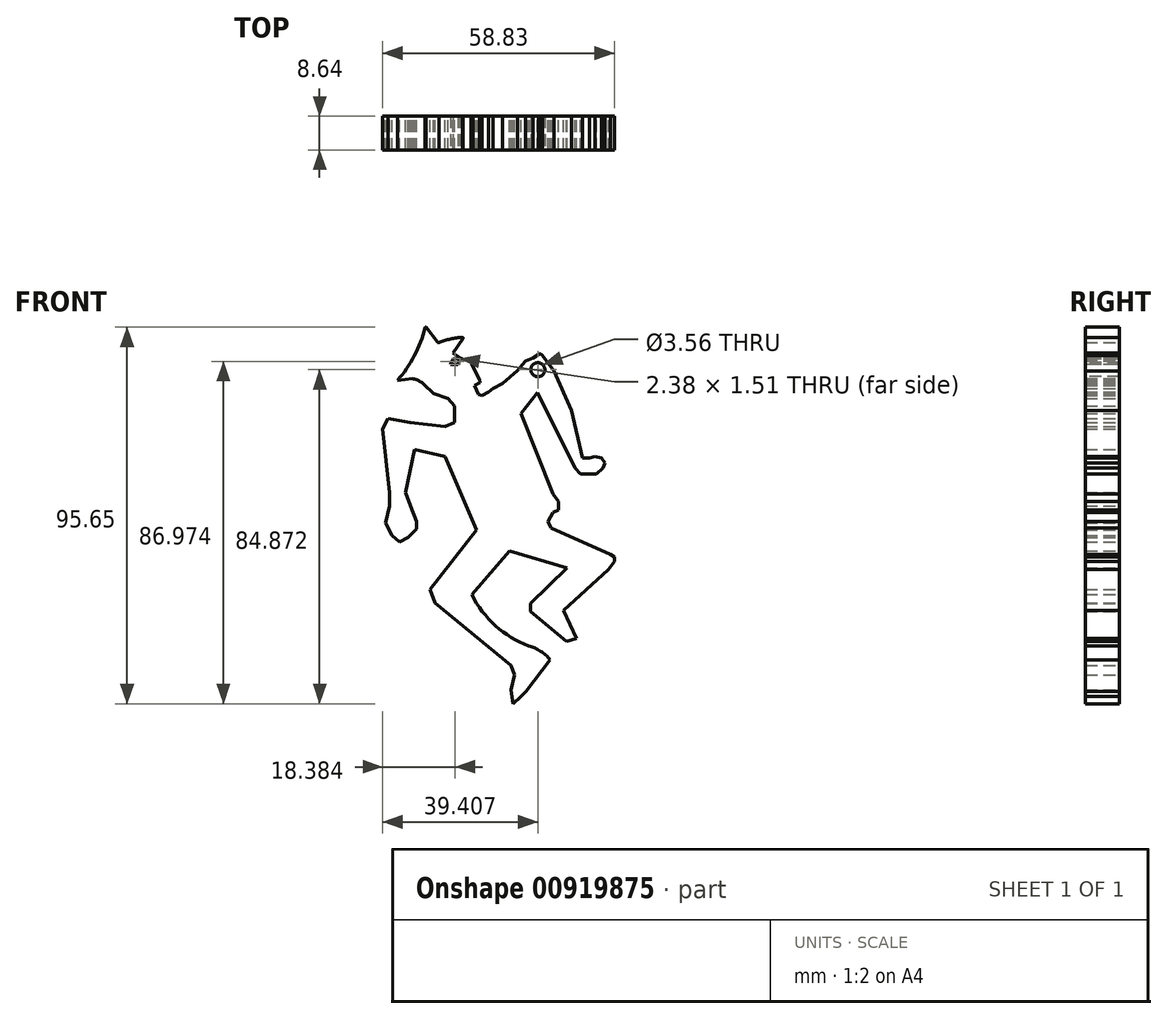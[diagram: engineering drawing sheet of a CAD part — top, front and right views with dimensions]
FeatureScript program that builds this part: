
annotation { "Feature Type Name" : "Feature", "Feature Type Description" : "" }
export const myFeature = defineFeature(function(context is Context, id is Id, definition is map)
    precondition{}
    {
        {
            var Q0;
            Q0=qCreatedBy(makeId("Front.planeOp"),FACE);
            var sketch = newSketch(context, id + "F0", { "sketchPlane" : qUnion([Q0])});
            skLineSegment(sketch, "E0", {"start": v(-42.46, 60.33) * mm, "end": v(-39.5, 56.54) * mm});
            skArc(sketch, "E1", {"start": v(-33.22, 57.79) * mm, "mid": v(-36.26, 57.36) * mm, "end": v(-39.19, 56.47) * mm});
            skLineSegment(sketch, "E2", {"start": v(-33.03, 57.41) * mm, "end": v(-35.53, 53.74) * mm});
            skLineSegment(sketch, "E3", {"start": v(-35.53, 53.74) * mm, "end": v(-33.9, 52.64) * mm});
            skArc(sketch, "E4", {"start": v(-33.9, 52.64) * mm, "mid": v(-32.51, 52.03) * mm, "end": v(-31, 51.97) * mm});
            skLineSegment(sketch, "E5", {"start": v(-30.57, 51.52) * mm, "end": v(-30.55, 51.48) * mm});
            skPoint(sketch, "E6.visualSharp", {"position": v(-29.06, 47.76) * mm});
            skPoint(sketch, "E7.visualSharp", {"position": v(-43.57, 61.76) * mm});
            skPoint(sketch, "E8.visualSharp", {"position": v(-39.37, 56.4) * mm});
            skLineSegment(sketch, "E8.filletArc", {"start": v(-39.5, 56.54) * mm, "end": v(-39.5, 56.54) * mm});
            skPoint(sketch, "E9.visualSharp", {"position": v(-32.76, 57.81) * mm});
            skArc(sketch, "E10", {"start": v(-49.73, 46.76) * mm, "mid": v(-45.43, 53.08) * mm, "end": v(-42.67, 60.2) * mm});
            skPoint(sketch, "E11.visualSharp", {"position": v(-45.9, 47.27) * mm});
            skPoint(sketch, "E12.start.orphan", {"position": v(-40.55, 47.27) * mm});
            skPoint(sketch, "E13.visualSharp", {"position": v(-44.94, 46.32) * mm});
            skLineSegment(sketch, "E14", {"start": v(-49.73, 46.76) * mm, "end": v(-45.9, 47.27) * mm});
            skLineSegment(sketch, "E15", {"start": v(-40.48, 43.49) * mm, "end": v(-36.87, 42.21) * mm});
            skPoint(sketch, "E16.visualSharp", {"position": v(-29.14, 39.42) * mm});
            skLineSegment(sketch, "E17", {"start": v(-19.25, 49.3) * mm, "end": v(-17.15, 51.78) * mm});
            skLineSegment(sketch, "E18", {"start": v(-13.91, 51.78) * mm, "end": v(-13.91, 51.78) * mm});
            skPoint(sketch, "E19.orphan", {"position": v(-29.14, 42.93) * mm});
            skLineSegment(sketch, "E20", {"start": v(-28.23, 42.93) * mm, "end": v(-26.53, 43.85) * mm});
            skLineSegment(sketch, "E21", {"start": v(-26.53, 43.85) * mm, "end": v(-25.41, 44.82) * mm});
            skPoint(sketch, "E22.start.orphan", {"position": v(-1.97, 42.93) * mm});
            skPoint(sketch, "E23.start.orphan", {"position": v(-1.97, 24.54) * mm});
            skPoint(sketch, "E24.end.orphan", {"position": v(0, 28.6) * mm});
            skLineSegment(sketch, "E25", {"start": v(-17.15, 51.78) * mm, "end": v(-17.16, 51.82) * mm});
            skLineSegment(sketch, "E26", {"start": v(-17.16, 51.82) * mm, "end": v(-17.16, 51.82) * mm});
            skLineSegment(sketch, "E27", {"start": v(-25.41, 44.82) * mm, "end": v(-23, 46) * mm});
            skLineSegment(sketch, "E28", {"start": v(-23, 46) * mm, "end": v(-19.25, 49.3) * mm});
            skPoint(sketch, "E29.start.orphan", {"position": v(-6.69, 30.24) * mm});
            skPoint(sketch, "E30.start.orphan", {"position": v(-2.5, 30.24) * mm});
            skLineSegment(sketch, "E31", {"start": v(-13.91, 54.64) * mm, "end": v(-13.91, 54.64) * mm});
            skLineSegment(sketch, "E32", {"start": v(-17.15, 51.78) * mm, "end": v(-15.28, 52.58) * mm});
            skLineSegment(sketch, "E33", {"start": v(-15.28, 52.58) * mm, "end": v(-13.91, 53.36) * mm});
            skLineSegment(sketch, "E34", {"start": v(-13.91, 53.36) * mm, "end": v(-13.78, 53.5) * mm});
            skLineSegment(sketch, "E35", {"start": v(-13.78, 53.5) * mm, "end": v(-13.54, 53.56) * mm});
            skLineSegment(sketch, "E36", {"start": v(-13.54, 53.56) * mm, "end": v(-13.2, 53.56) * mm});
            skLineSegment(sketch, "E37", {"start": v(-13.2, 53.56) * mm, "end": v(-12.83, 53.21) * mm});
            skLineSegment(sketch, "E38", {"start": v(-12.83, 53.21) * mm, "end": v(-9.9, 49.27) * mm});
            skLineSegment(sketch, "E39", {"start": v(-9.9, 49.27) * mm, "end": v(-5.47, 39.16) * mm});
            skPoint(sketch, "E40.end.orphan", {"position": v(-14.16, 44.09) * mm});
            skLineSegment(sketch, "E41", {"start": v(-14.16, 43.7) * mm, "end": v(-18.27, 38.38) * mm});
            skPoint(sketch, "E42.end.orphan", {"position": v(-5.47, 13.93) * mm});
            skLineSegment(sketch, "E43", {"start": v(-18.27, 38.38) * mm, "end": v(-10.19, 17.96) * mm});
            skLineSegment(sketch, "E44", {"start": v(-10.19, 17.96) * mm, "end": v(-8.77, 16.01) * mm});
            skLineSegment(sketch, "E45", {"start": v(-8.77, 16.01) * mm, "end": v(-8.77, 13.93) * mm});
            skLineSegment(sketch, "E46", {"start": v(-8.77, 13.93) * mm, "end": v(-10.19, 13.34) * mm});
            skLineSegment(sketch, "E47", {"start": v(-10.19, 13.34) * mm, "end": v(-11.4, 11.02) * mm});
            skLineSegment(sketch, "E48", {"start": v(-11.4, 11.02) * mm, "end": v(-10.7, 9.36) * mm});
            skLineSegment(sketch, "E49", {"start": v(-10.7, 9.36) * mm, "end": v(4.46, 2.67) * mm});
            skLineSegment(sketch, "E50", {"start": v(4.46, 2.67) * mm, "end": v(5.39, 1.92) * mm});
            skLineSegment(sketch, "E51", {"start": v(5.39, 1.92) * mm, "end": v(5.39, 0.85) * mm});
            skLineSegment(sketch, "E52", {"start": v(5.39, 0.85) * mm, "end": v(3.87, -1.18) * mm});
            skLineSegment(sketch, "E53", {"start": v(3.87, -1.18) * mm, "end": v(-7.5, -11.64) * mm});
            skLineSegment(sketch, "E54", {"start": v(-7.5, -11.64) * mm, "end": v(-4.25, -18.67) * mm});
            skLineSegment(sketch, "E55", {"start": v(-4.25, -18.67) * mm, "end": v(-6.73, -19.54) * mm});
            skLineSegment(sketch, "E56", {"start": v(-6.73, -19.54) * mm, "end": v(-15.96, -11.83) * mm});
            skLineSegment(sketch, "E57", {"start": v(-15.96, -11.83) * mm, "end": v(-15.96, -9.78) * mm});
            skLineSegment(sketch, "E58", {"start": v(-15.96, -9.78) * mm, "end": v(-6.67, -0.79) * mm});
            skLineSegment(sketch, "E59", {"start": v(-6.67, -0.79) * mm, "end": v(-21.2, 3.47) * mm});
            skLineSegment(sketch, "E60", {"start": v(-21.2, 3.47) * mm, "end": v(-30.77, -7.6) * mm});
            skArc(sketch, "E61", {"start": v(-30.77, -7.6) * mm, "mid": v(-24.82, -15.5) * mm, "end": v(-16.34, -20.6) * mm});
            skArc(sketch, "E62", {"start": v(-10.9, -24.14) * mm, "mid": v(-13.36, -21.97) * mm, "end": v(-16.34, -20.6) * mm});
            skPoint(sketch, "E63.end.orphan", {"position": v(-19.53, -33.46) * mm});
            skLineSegment(sketch, "E64", {"start": v(-10.9, -24.14) * mm, "end": v(-17, -32.15) * mm});
            skLineSegment(sketch, "E65", {"start": v(-20.92, -25.62) * mm, "end": v(-40.11, -9.66) * mm});
            skLineSegment(sketch, "E66", {"start": v(-40.11, -9.66) * mm, "end": v(-41.4, -6.32) * mm});
            skLineSegment(sketch, "E67", {"start": v(-41.4, -6.32) * mm, "end": v(-29.57, 8.87) * mm});
            skLineSegment(sketch, "E68", {"start": v(-29.57, 8.87) * mm, "end": v(-37.63, 27.46) * mm});
            skLineSegment(sketch, "E69", {"start": v(-18.36, -33.46) * mm, "end": v(-17, -32.15) * mm});
            skLineSegment(sketch, "E70", {"start": v(-20.92, -25.62) * mm, "end": v(-19.96, -28) * mm});
            skLineSegment(sketch, "E71", {"start": v(-19.96, -28) * mm, "end": v(-20.92, -31.85) * mm});
            skLineSegment(sketch, "E72", {"start": v(-20.92, -31.85) * mm, "end": v(-20.4, -35.3) * mm});
            skLineSegment(sketch, "E73", {"start": v(-20.4, -35.3) * mm, "end": v(-18.36, -33.46) * mm});
            skLineSegment(sketch, "E74", {"start": v(-37.63, 27.46) * mm, "end": v(-45.33, 29.3) * mm});
            skLineSegment(sketch, "E75", {"start": v(-45.33, 29.3) * mm, "end": v(-47.6, 18.32) * mm});
            skPoint(sketch, "E76.end.orphan", {"position": v(-43.53, 6.93) * mm});
            skPoint(sketch, "E77.start.orphan", {"position": v(-54.21, 14.98) * mm});
            skPoint(sketch, "E78.end.orphan", {"position": v(-45.15, 18.32) * mm});
            skPoint(sketch, "E79.start.orphan", {"position": v(-43.35, 14.98) * mm});
            skPoint(sketch, "E80.end.orphan", {"position": v(-43.53, 14.6) * mm});
            skLineSegment(sketch, "E81", {"start": v(-36.87, 42.21) * mm, "end": v(-35.27, 40.35) * mm});
            skLineSegment(sketch, "E82", {"start": v(-35.27, 40.35) * mm, "end": v(-35.27, 36.17) * mm});
            skPoint(sketch, "E83.end.orphan", {"position": v(-50.83, 40.35) * mm});
            skLineSegment(sketch, "E84", {"start": v(-35.27, 36.17) * mm, "end": v(-37.58, 35.16) * mm});
            skLineSegment(sketch, "E85", {"start": v(-37.58, 35.16) * mm, "end": v(-46.56, 36.17) * mm});
            skLineSegment(sketch, "E86", {"start": v(-46.56, 36.17) * mm, "end": v(-52.05, 37.2) * mm});
            skLineSegment(sketch, "E87", {"start": v(-52.05, 37.2) * mm, "end": v(-53.44, 34.54) * mm});
            skLineSegment(sketch, "E88", {"start": v(-53.44, 34.54) * mm, "end": v(-51.66, 18.3) * mm});
            skLineSegment(sketch, "E89", {"start": v(-51.66, 18.3) * mm, "end": v(-51.66, 14.98) * mm});
            skLineSegment(sketch, "E90", {"start": v(-51.66, 14.98) * mm, "end": v(-52.72, 10.64) * mm});
            skLineSegment(sketch, "E91", {"start": v(-52.72, 10.64) * mm, "end": v(-51.02, 7.45) * mm});
            skLineSegment(sketch, "E92", {"start": v(-51.02, 7.45) * mm, "end": v(-49.1, 5.75) * mm});
            skLineSegment(sketch, "E93", {"start": v(-49.1, 5.75) * mm, "end": v(-47, 6.95) * mm});
            skLineSegment(sketch, "E94", {"start": v(-47, 6.95) * mm, "end": v(-44.9, 9.05) * mm});
            skLineSegment(sketch, "E95", {"start": v(-44.9, 9.05) * mm, "end": v(-44.9, 11.01) * mm});
            skLineSegment(sketch, "E96", {"start": v(-44.9, 11.01) * mm, "end": v(-46.4, 14.98) * mm});
            skLineSegment(sketch, "E97", {"start": v(-46.4, 14.98) * mm, "end": v(-47.6, 18.32) * mm});
            skPoint(sketch, "E98.start.orphan", {"position": v(-31.47, 26.33) * mm});
            skLineSegment(sketch, "E99", {"start": v(-14.16, 43.7) * mm, "end": v(-4.64, 24.54) * mm});
            skPoint(sketch, "E100.start.orphan", {"position": v(-2.33, 26.33) * mm});
            skPoint(sketch, "E101.start.orphan", {"position": v(-1.97, 29.68) * mm});
            skLineSegment(sketch, "E102", {"start": v(-4.64, 24.54) * mm, "end": v(-3.26, 23.05) * mm});
            skLineSegment(sketch, "E103", {"start": v(-3.26, 23.05) * mm, "end": v(-1.56, 23.05) * mm});
            skLineSegment(sketch, "E104", {"start": v(-1.56, 23.05) * mm, "end": v(0.9, 23.05) * mm});
            skLineSegment(sketch, "E105", {"start": v(0.9, 23.05) * mm, "end": v(2.47, 24.54) * mm});
            skLineSegment(sketch, "E106", {"start": v(2.47, 24.54) * mm, "end": v(3, 25.85) * mm});
            skLineSegment(sketch, "E107", {"start": v(3, 25.85) * mm, "end": v(2.17, 27.06) * mm});
            skLineSegment(sketch, "E108", {"start": v(2.17, 27.06) * mm, "end": v(0.49, 27.47) * mm});
            skLineSegment(sketch, "E109", {"start": v(0.49, 27.47) * mm, "end": v(-0.94, 27.06) * mm});
            skLineSegment(sketch, "E110", {"start": v(-0.94, 27.06) * mm, "end": v(-2.73, 27.06) * mm});
            skLineSegment(sketch, "E111", {"start": v(-2.73, 27.06) * mm, "end": v(-5.47, 39.16) * mm});
            skArc(sketch, "E112", {"start": v(-33.03, 57.41) * mm, "mid": v(-33.02, 57.66) * mm, "end": v(-33.22, 57.79) * mm});
            skArc(sketch, "E113", {"start": v(-39.5, 56.54) * mm, "mid": v(-39.35, 56.45) * mm, "end": v(-39.19, 56.47) * mm});
            skArc(sketch, "E114", {"start": v(-42.46, 60.33) * mm, "mid": v(-42.6, 60.32) * mm, "end": v(-42.67, 60.2) * mm});
            skLineSegment(sketch, "E115", {"start": v(-30.18, 45.57) * mm, "end": v(-29.06, 43.3) * mm});
            skLineSegment(sketch, "E116", {"start": v(-29.06, 43.3) * mm, "end": v(-28.23, 42.93) * mm});
            skPoint(sketch, "E117.orphan", {"position": v(-45.15, 46.4) * mm});
            skLineSegment(sketch, "E118", {"start": v(-40.48, 43.49) * mm, "end": v(-43.03, 45.87) * mm});
            skArc(sketch, "E119", {"start": v(-43.03, 45.87) * mm, "mid": v(-44.36, 46.78) * mm, "end": v(-45.9, 47.27) * mm});
            skPoint(sketch, "E120.visualSharp", {"position": v(-31.27, 47.76) * mm});
            skPoint(sketch, "E121.visualSharp", {"position": v(-28.47, 46.3) * mm});
            skPoint(sketch, "E122.visualSharp", {"position": v(-30.49, 52.08) * mm});
            skLineSegment(sketch, "E123", {"start": v(-30.18, 45.57) * mm, "end": v(-28.77, 46.27) * mm});
            skLineSegment(sketch, "E124", {"start": v(-28.8, 47) * mm, "end": v(-28.77, 46.27) * mm});
            skLineSegment(sketch, "E125", {"start": v(-30.45, 52.08) * mm, "end": v(-31, 51.97) * mm});
            skArc(sketch, "E126", {"start": v(-30.88, 50.96) * mm, "mid": v(-30.55, 51.47) * mm, "end": v(-30.45, 52.08) * mm});
            skLineSegment(sketch, "E127", {"start": v(-30.88, 50.96) * mm, "end": v(-28.8, 47) * mm});
            skSolve(sketch);
        }
        {
            var Q0;
            Q0 = qSketchRegion(id + "F0", true);
            extrude(context, id + "F1", {"entities" : qUnion([Q0]), "depth" : 8.64 * mm, "offsetDistance" : 25.4 * mm});
        }
        {
            var Q0;
            Q0=makeQuery(id+"F1.opExtrude","CAP_FACE",FACE,{"disambiguationData":[OSD([sQuery(id+"F0.wireOp",EDGE,"E0"),sQuery(id+"F0.wireOp",EDGE,"E1"),sQuery(id+"F0.wireOp",EDGE,"E2"),sQuery(id+"F0.wireOp",EDGE,"E3"),sQuery(id+"F0.wireOp",EDGE,"E4"),sQuery(id+"F0.wireOp",EDGE,"ytfFSvoo-UfpH-094h-fiFI-G8Bk86kOsi4I"),sQuery(id+"F0.wireOp",EDGE,"E5"),sQuery(id+"F0.wireOp",EDGE,"E10"),sQuery(id+"F0.wireOp",EDGE,"E14"),sQuery(id+"F0.wireOp",EDGE,"E15"),sQuery(id+"F0.wireOp",EDGE,"E17"),sQuery(id+"F0.wireOp",EDGE,"u4SKIOBJ-AyiB-IBHR-kLHR-u4tUaS0mDR8Y"),sQuery(id+"F0.wireOp",EDGE,"E20"),sQuery(id+"F0.wireOp",EDGE,"E21"),sQuery(id+"F0.wireOp",EDGE,"E27"),sQuery(id+"F0.wireOp",EDGE,"E28"),sQuery(id+"F0.wireOp",EDGE,"E32"),sQuery(id+"F0.wireOp",EDGE,"E33"),sQuery(id+"F0.wireOp",EDGE,"E34"),sQuery(id+"F0.wireOp",EDGE,"E35"),sQuery(id+"F0.wireOp",EDGE,"E36"),sQuery(id+"F0.wireOp",EDGE,"E37"),sQuery(id+"F0.wireOp",EDGE,"E38"),sQuery(id+"F0.wireOp",EDGE,"E39"),sQuery(id+"F0.wireOp",EDGE,"E41"),sQuery(id+"F0.wireOp",EDGE,"E43"),sQuery(id+"F0.wireOp",EDGE,"E44"),sQuery(id+"F0.wireOp",EDGE,"E45"),sQuery(id+"F0.wireOp",EDGE,"E46"),sQuery(id+"F0.wireOp",EDGE,"E47"),sQuery(id+"F0.wireOp",EDGE,"E48"),sQuery(id+"F0.wireOp",EDGE,"E49"),sQuery(id+"F0.wireOp",EDGE,"E50"),sQuery(id+"F0.wireOp",EDGE,"E51"),sQuery(id+"F0.wireOp",EDGE,"E52"),sQuery(id+"F0.wireOp",EDGE,"E53"),sQuery(id+"F0.wireOp",EDGE,"E54"),sQuery(id+"F0.wireOp",EDGE,"E55"),sQuery(id+"F0.wireOp",EDGE,"E56"),sQuery(id+"F0.wireOp",EDGE,"E57"),sQuery(id+"F0.wireOp",EDGE,"E58"),sQuery(id+"F0.wireOp",EDGE,"E59"),sQuery(id+"F0.wireOp",EDGE,"E60"),sQuery(id+"F0.wireOp",EDGE,"E61"),sQuery(id+"F0.wireOp",EDGE,"E62"),sQuery(id+"F0.wireOp",EDGE,"E64"),sQuery(id+"F0.wireOp",EDGE,"E65"),sQuery(id+"F0.wireOp",EDGE,"E66"),sQuery(id+"F0.wireOp",EDGE,"E67"),sQuery(id+"F0.wireOp",EDGE,"E68"),sQuery(id+"F0.wireOp",EDGE,"E69"),sQuery(id+"F0.wireOp",EDGE,"E70"),sQuery(id+"F0.wireOp",EDGE,"E71"),sQuery(id+"F0.wireOp",EDGE,"E72"),sQuery(id+"F0.wireOp",EDGE,"E73"),sQuery(id+"F0.wireOp",EDGE,"E74"),sQuery(id+"F0.wireOp",EDGE,"E75"),sQuery(id+"F0.wireOp",EDGE,"E81"),sQuery(id+"F0.wireOp",EDGE,"E82"),sQuery(id+"F0.wireOp",EDGE,"E84"),sQuery(id+"F0.wireOp",EDGE,"E85"),sQuery(id+"F0.wireOp",EDGE,"E86"),sQuery(id+"F0.wireOp",EDGE,"E87"),sQuery(id+"F0.wireOp",EDGE,"E88"),sQuery(id+"F0.wireOp",EDGE,"E89"),sQuery(id+"F0.wireOp",EDGE,"E90"),sQuery(id+"F0.wireOp",EDGE,"E91"),sQuery(id+"F0.wireOp",EDGE,"E92"),sQuery(id+"F0.wireOp",EDGE,"E93"),sQuery(id+"F0.wireOp",EDGE,"E94"),sQuery(id+"F0.wireOp",EDGE,"E95"),sQuery(id+"F0.wireOp",EDGE,"E96"),sQuery(id+"F0.wireOp",EDGE,"E97"),sQuery(id+"F0.wireOp",EDGE,"E99"),sQuery(id+"F0.wireOp",EDGE,"E102"),sQuery(id+"F0.wireOp",EDGE,"E103"),sQuery(id+"F0.wireOp",EDGE,"E104"),sQuery(id+"F0.wireOp",EDGE,"E105"),sQuery(id+"F0.wireOp",EDGE,"E106"),sQuery(id+"F0.wireOp",EDGE,"E107"),sQuery(id+"F0.wireOp",EDGE,"E108"),sQuery(id+"F0.wireOp",EDGE,"E109"),sQuery(id+"F0.wireOp",EDGE,"E110"),sQuery(id+"F0.wireOp",EDGE,"E111"),sQuery(id+"F0.wireOp",EDGE,"E112"),sQuery(id+"F0.wireOp",EDGE,"E113"),sQuery(id+"F0.wireOp",EDGE,"E114"),sQuery(id+"F0.wireOp",EDGE,"E115"),sQuery(id+"F0.wireOp",EDGE,"E116"),sQuery(id+"F0.wireOp",EDGE,"E118"),sQuery(id+"F0.wireOp",EDGE,"E119")])],"isStart":false});
            var sketch = newSketch(context, id + "F2", { "sketchPlane" : qUnion([Q0])});
            skPoint(sketch, "E128", {"position": v(-14.03, 49.56) * mm});
            skSolve(sketch);
        }
        {
            var Q0;
            Q0=sQuery(id+"F2.wireOp",VERTEX,"E128");
            var Q1;
            Q1=makeQuery(id+"F1.opExtrude","SWEPT_BODY",BODY,{"disambiguationData":[OSD([sQuery(id+"F0.wireOp",EDGE,"E0"),sQuery(id+"F0.wireOp",EDGE,"E1"),sQuery(id+"F0.wireOp",EDGE,"E2"),sQuery(id+"F0.wireOp",EDGE,"E3"),sQuery(id+"F0.wireOp",EDGE,"E4"),sQuery(id+"F0.wireOp",EDGE,"ytfFSvoo-UfpH-094h-fiFI-G8Bk86kOsi4I"),sQuery(id+"F0.wireOp",EDGE,"E5"),sQuery(id+"F0.wireOp",EDGE,"E10"),sQuery(id+"F0.wireOp",EDGE,"E14"),sQuery(id+"F0.wireOp",EDGE,"E15"),sQuery(id+"F0.wireOp",EDGE,"E17"),sQuery(id+"F0.wireOp",EDGE,"u4SKIOBJ-AyiB-IBHR-kLHR-u4tUaS0mDR8Y"),sQuery(id+"F0.wireOp",EDGE,"E20"),sQuery(id+"F0.wireOp",EDGE,"E21"),sQuery(id+"F0.wireOp",EDGE,"E27"),sQuery(id+"F0.wireOp",EDGE,"E28"),sQuery(id+"F0.wireOp",EDGE,"E32"),sQuery(id+"F0.wireOp",EDGE,"E33"),sQuery(id+"F0.wireOp",EDGE,"E34"),sQuery(id+"F0.wireOp",EDGE,"E35"),sQuery(id+"F0.wireOp",EDGE,"E36"),sQuery(id+"F0.wireOp",EDGE,"E37"),sQuery(id+"F0.wireOp",EDGE,"E38"),sQuery(id+"F0.wireOp",EDGE,"E39"),sQuery(id+"F0.wireOp",EDGE,"E41"),sQuery(id+"F0.wireOp",EDGE,"E43"),sQuery(id+"F0.wireOp",EDGE,"E44"),sQuery(id+"F0.wireOp",EDGE,"E45"),sQuery(id+"F0.wireOp",EDGE,"E46"),sQuery(id+"F0.wireOp",EDGE,"E47"),sQuery(id+"F0.wireOp",EDGE,"E48"),sQuery(id+"F0.wireOp",EDGE,"E49"),sQuery(id+"F0.wireOp",EDGE,"E50"),sQuery(id+"F0.wireOp",EDGE,"E51"),sQuery(id+"F0.wireOp",EDGE,"E52"),sQuery(id+"F0.wireOp",EDGE,"E53"),sQuery(id+"F0.wireOp",EDGE,"E54"),sQuery(id+"F0.wireOp",EDGE,"E55"),sQuery(id+"F0.wireOp",EDGE,"E56"),sQuery(id+"F0.wireOp",EDGE,"E57"),sQuery(id+"F0.wireOp",EDGE,"E58"),sQuery(id+"F0.wireOp",EDGE,"E59"),sQuery(id+"F0.wireOp",EDGE,"E60"),sQuery(id+"F0.wireOp",EDGE,"E61"),sQuery(id+"F0.wireOp",EDGE,"E62"),sQuery(id+"F0.wireOp",EDGE,"E64"),sQuery(id+"F0.wireOp",EDGE,"E65"),sQuery(id+"F0.wireOp",EDGE,"E66"),sQuery(id+"F0.wireOp",EDGE,"E67"),sQuery(id+"F0.wireOp",EDGE,"E68"),sQuery(id+"F0.wireOp",EDGE,"E69"),sQuery(id+"F0.wireOp",EDGE,"E70"),sQuery(id+"F0.wireOp",EDGE,"E71"),sQuery(id+"F0.wireOp",EDGE,"E72"),sQuery(id+"F0.wireOp",EDGE,"E73"),sQuery(id+"F0.wireOp",EDGE,"E74"),sQuery(id+"F0.wireOp",EDGE,"E75"),sQuery(id+"F0.wireOp",EDGE,"E81"),sQuery(id+"F0.wireOp",EDGE,"E82"),sQuery(id+"F0.wireOp",EDGE,"E84"),sQuery(id+"F0.wireOp",EDGE,"E85"),sQuery(id+"F0.wireOp",EDGE,"E86"),sQuery(id+"F0.wireOp",EDGE,"E87"),sQuery(id+"F0.wireOp",EDGE,"E88"),sQuery(id+"F0.wireOp",EDGE,"E89"),sQuery(id+"F0.wireOp",EDGE,"E90"),sQuery(id+"F0.wireOp",EDGE,"E91"),sQuery(id+"F0.wireOp",EDGE,"E92"),sQuery(id+"F0.wireOp",EDGE,"E93"),sQuery(id+"F0.wireOp",EDGE,"E94"),sQuery(id+"F0.wireOp",EDGE,"E95"),sQuery(id+"F0.wireOp",EDGE,"E96"),sQuery(id+"F0.wireOp",EDGE,"E97"),sQuery(id+"F0.wireOp",EDGE,"E99"),sQuery(id+"F0.wireOp",EDGE,"E102"),sQuery(id+"F0.wireOp",EDGE,"E103"),sQuery(id+"F0.wireOp",EDGE,"E104"),sQuery(id+"F0.wireOp",EDGE,"E105"),sQuery(id+"F0.wireOp",EDGE,"E106"),sQuery(id+"F0.wireOp",EDGE,"E107"),sQuery(id+"F0.wireOp",EDGE,"E108"),sQuery(id+"F0.wireOp",EDGE,"E109"),sQuery(id+"F0.wireOp",EDGE,"E110"),sQuery(id+"F0.wireOp",EDGE,"E111"),sQuery(id+"F0.wireOp",EDGE,"E112"),sQuery(id+"F0.wireOp",EDGE,"E113"),sQuery(id+"F0.wireOp",EDGE,"E114"),sQuery(id+"F0.wireOp",EDGE,"E115"),sQuery(id+"F0.wireOp",EDGE,"E116"),sQuery(id+"F0.wireOp",EDGE,"E118"),sQuery(id+"F0.wireOp",EDGE,"E119")])]});
            hole(context, id + "F3", {"style" : HoleStyle.SIMPLE, "endStyle" : HoleEndStyle.THROUGH, "holeDiameter" : 3.56 * mm, "majorDiameter" : 6.35 * mm, "isTappedThrough" : true, "tappedDepth" : 12.7 * mm, "tapClearance" : 3, "locations" : qUnion([Q0]), "scope" : qUnion([Q1])});
        }
        {
            var Q0;
            Q0=makeQuery(id+"F1.opExtrude","CAP_FACE",FACE,{"disambiguationData":[OSD([sQuery(id+"F0.wireOp",EDGE,"E0"),sQuery(id+"F0.wireOp",EDGE,"E1"),sQuery(id+"F0.wireOp",EDGE,"E2"),sQuery(id+"F0.wireOp",EDGE,"E3"),sQuery(id+"F0.wireOp",EDGE,"E4"),sQuery(id+"F0.wireOp",EDGE,"ytfFSvoo-UfpH-094h-fiFI-G8Bk86kOsi4I"),sQuery(id+"F0.wireOp",EDGE,"E5"),sQuery(id+"F0.wireOp",EDGE,"E10"),sQuery(id+"F0.wireOp",EDGE,"E14"),sQuery(id+"F0.wireOp",EDGE,"E15"),sQuery(id+"F0.wireOp",EDGE,"E17"),sQuery(id+"F0.wireOp",EDGE,"u4SKIOBJ-AyiB-IBHR-kLHR-u4tUaS0mDR8Y"),sQuery(id+"F0.wireOp",EDGE,"E20"),sQuery(id+"F0.wireOp",EDGE,"E21"),sQuery(id+"F0.wireOp",EDGE,"E27"),sQuery(id+"F0.wireOp",EDGE,"E28"),sQuery(id+"F0.wireOp",EDGE,"E32"),sQuery(id+"F0.wireOp",EDGE,"E33"),sQuery(id+"F0.wireOp",EDGE,"E34"),sQuery(id+"F0.wireOp",EDGE,"E35"),sQuery(id+"F0.wireOp",EDGE,"E36"),sQuery(id+"F0.wireOp",EDGE,"E37"),sQuery(id+"F0.wireOp",EDGE,"E38"),sQuery(id+"F0.wireOp",EDGE,"E39"),sQuery(id+"F0.wireOp",EDGE,"E41"),sQuery(id+"F0.wireOp",EDGE,"E43"),sQuery(id+"F0.wireOp",EDGE,"E44"),sQuery(id+"F0.wireOp",EDGE,"E45"),sQuery(id+"F0.wireOp",EDGE,"E46"),sQuery(id+"F0.wireOp",EDGE,"E47"),sQuery(id+"F0.wireOp",EDGE,"E48"),sQuery(id+"F0.wireOp",EDGE,"E49"),sQuery(id+"F0.wireOp",EDGE,"E50"),sQuery(id+"F0.wireOp",EDGE,"E51"),sQuery(id+"F0.wireOp",EDGE,"E52"),sQuery(id+"F0.wireOp",EDGE,"E53"),sQuery(id+"F0.wireOp",EDGE,"E54"),sQuery(id+"F0.wireOp",EDGE,"E55"),sQuery(id+"F0.wireOp",EDGE,"E56"),sQuery(id+"F0.wireOp",EDGE,"E57"),sQuery(id+"F0.wireOp",EDGE,"E58"),sQuery(id+"F0.wireOp",EDGE,"E59"),sQuery(id+"F0.wireOp",EDGE,"E60"),sQuery(id+"F0.wireOp",EDGE,"E61"),sQuery(id+"F0.wireOp",EDGE,"E62"),sQuery(id+"F0.wireOp",EDGE,"E64"),sQuery(id+"F0.wireOp",EDGE,"E65"),sQuery(id+"F0.wireOp",EDGE,"E66"),sQuery(id+"F0.wireOp",EDGE,"E67"),sQuery(id+"F0.wireOp",EDGE,"E68"),sQuery(id+"F0.wireOp",EDGE,"E69"),sQuery(id+"F0.wireOp",EDGE,"E70"),sQuery(id+"F0.wireOp",EDGE,"E71"),sQuery(id+"F0.wireOp",EDGE,"E72"),sQuery(id+"F0.wireOp",EDGE,"E73"),sQuery(id+"F0.wireOp",EDGE,"E74"),sQuery(id+"F0.wireOp",EDGE,"E75"),sQuery(id+"F0.wireOp",EDGE,"E81"),sQuery(id+"F0.wireOp",EDGE,"E82"),sQuery(id+"F0.wireOp",EDGE,"E84"),sQuery(id+"F0.wireOp",EDGE,"E85"),sQuery(id+"F0.wireOp",EDGE,"E86"),sQuery(id+"F0.wireOp",EDGE,"E87"),sQuery(id+"F0.wireOp",EDGE,"E88"),sQuery(id+"F0.wireOp",EDGE,"E89"),sQuery(id+"F0.wireOp",EDGE,"E90"),sQuery(id+"F0.wireOp",EDGE,"E91"),sQuery(id+"F0.wireOp",EDGE,"E92"),sQuery(id+"F0.wireOp",EDGE,"E93"),sQuery(id+"F0.wireOp",EDGE,"E94"),sQuery(id+"F0.wireOp",EDGE,"E95"),sQuery(id+"F0.wireOp",EDGE,"E96"),sQuery(id+"F0.wireOp",EDGE,"E97"),sQuery(id+"F0.wireOp",EDGE,"E99"),sQuery(id+"F0.wireOp",EDGE,"E102"),sQuery(id+"F0.wireOp",EDGE,"E103"),sQuery(id+"F0.wireOp",EDGE,"E104"),sQuery(id+"F0.wireOp",EDGE,"E105"),sQuery(id+"F0.wireOp",EDGE,"E106"),sQuery(id+"F0.wireOp",EDGE,"E107"),sQuery(id+"F0.wireOp",EDGE,"E108"),sQuery(id+"F0.wireOp",EDGE,"E109"),sQuery(id+"F0.wireOp",EDGE,"E110"),sQuery(id+"F0.wireOp",EDGE,"E111"),sQuery(id+"F0.wireOp",EDGE,"E112"),sQuery(id+"F0.wireOp",EDGE,"E113"),sQuery(id+"F0.wireOp",EDGE,"E114"),sQuery(id+"F0.wireOp",EDGE,"E115"),sQuery(id+"F0.wireOp",EDGE,"E116"),sQuery(id+"F0.wireOp",EDGE,"E118"),sQuery(id+"F0.wireOp",EDGE,"E119")])],"isStart":false});
            var sketch = newSketch(context, id + "F4", { "sketchPlane" : qUnion([Q0])});
            skLineSegment(sketch, "E129", {"start": v(-34.37, 50.9) * mm, "end": v(-36.25, 50.9) * mm});
            skLineSegment(sketch, "E130", {"start": v(-36.25, 50.9) * mm, "end": v(-35.53, 52.3) * mm});
            skLineSegment(sketch, "E131", {"start": v(-35.53, 52.3) * mm, "end": v(-33.87, 52.42) * mm});
            skLineSegment(sketch, "E132", {"start": v(-33.87, 52.42) * mm, "end": v(-34.37, 50.9) * mm});
            skSolve(sketch);
        }
        {
            var Q0;
            Q0=makeQuery(id+"F4.imprint","IMPRINT",FACE,{"disambiguationData":[TD([[makeQuery(id+"F4.imprint","IMPRINT",EDGE,{"derivedFrom":sQuery(id+"F4.wireOp",EDGE,"E129")}),-1.0]])]});
            extrude(context, id + "F5", {"entities" : qUnion([Q0]), "operationType" : NewBodyOperationType.REMOVE, "oppositeDirection" : true, "depth" : 25.4 * mm, "offsetDistance" : 25.4 * mm});
        }
    });
